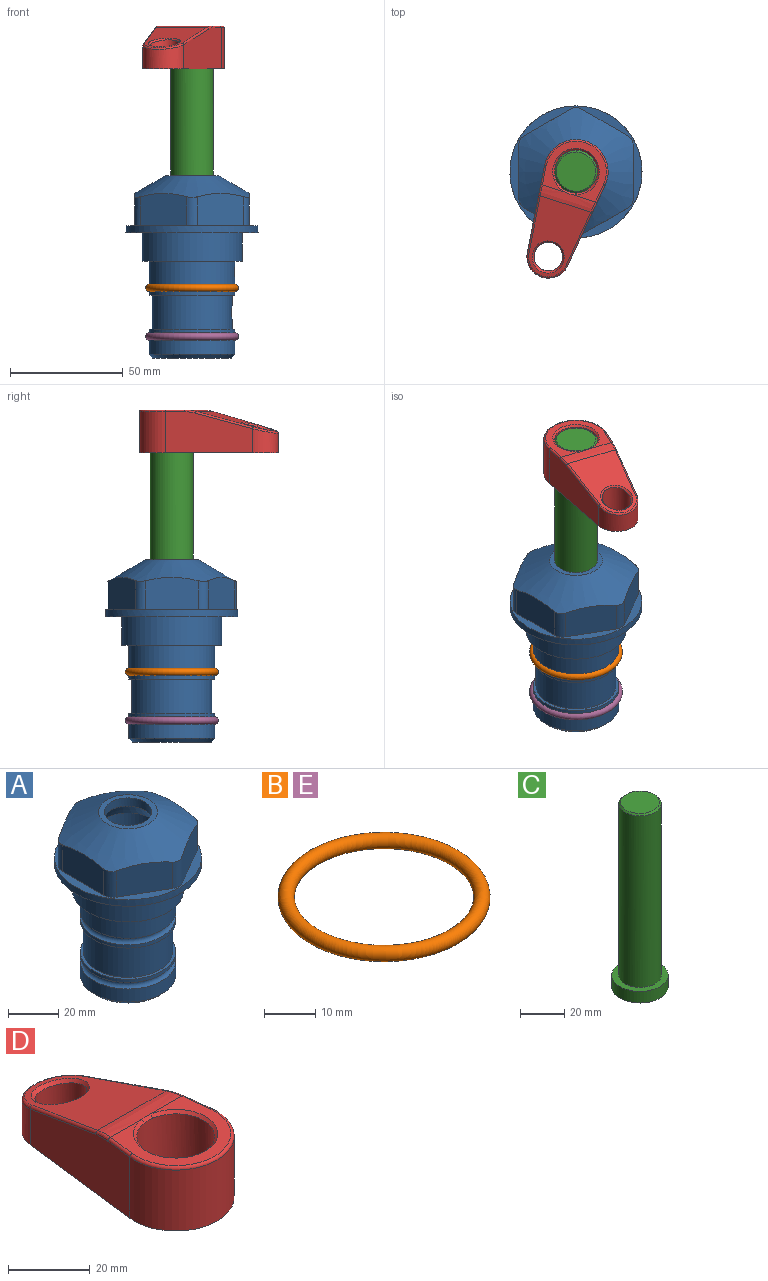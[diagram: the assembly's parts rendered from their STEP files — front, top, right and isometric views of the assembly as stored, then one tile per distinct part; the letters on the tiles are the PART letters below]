
ASSEMBLY  parts=5 mates=4
PART A: 36 faces, bbox 58.7x58.7x81 mm
  f0: cylinder r=17.78mm len=35.56mm, axis (0,0,1), area 1670.8mm2, adj f23,f24,f31
  f1: cylinder r=19.05mm len=38.1mm, axis (0,0,1), area 1191.9mm2, adj f26,f27,f30
  f2: plane 58.66x58.66mm, normal (0,0,-1), area 1150.6mm2, adj f3,f28
  f3: cylinder r=29.33mm len=58.66mm, axis (0,0,-1), area 585.1mm2, adj f2,f4
  f4: plane 58.66x58.66mm, normal (0,0,1), area 475.9mm2, adj f3,f5,f6,f7,f8,f9,f10,f11
  f5: plane 20.32x14.34mm, normal (-0.5,0.87,0), area 324.4mm2, adj f4,f15,f16,f17
  f6: plane 20.32x14.34mm, normal (0.5,0.87,0), area 324.4mm2, adj f4,f14,f15,f17
  f7: plane 23.48x14.34mm, normal (1,0,0), area 324.4mm2, adj f4,f13,f14,f17
  f8: plane 20.32x14.34mm, normal (0.5,-0.87,0), area 324.4mm2, adj f4,f12,f13,f17
  f9: plane 20.32x14.34mm, normal (-0.5,-0.87,0), area 324.4mm2, adj f4,f11,f12,f17
  f10: plane 23.48x14.34mm, normal (-1,0,0), area 324.4mm2, adj f4,f11,f16,f17
  f11: cylinder r=5.08mm len=12.85mm, axis (0,0,-1), area 67.2mm2, adj f4,f9,f10,f17
  f12: cylinder r=5.08mm len=12.85mm, axis (0,0,-1), area 67.2mm2, adj f4,f8,f9,f17
  f13: cylinder r=5.08mm len=12.85mm, axis (0,0,-1), area 67.2mm2, adj f4,f7,f8,f17
  f14: cylinder r=5.08mm len=12.85mm, axis (0,0,-1), area 67.2mm2, adj f4,f6,f7,f17
  f15: cylinder r=5.08mm len=12.85mm, axis (0,0,-1), area 67.2mm2, adj f4,f5,f6,f17
  f16: cylinder r=5.08mm len=12.85mm, axis (0,0,-1), area 67.2mm2, adj f4,f5,f10,f17
  f17: cone r=11.73mm half-angle=60deg, axis (0,0,-1), area 2071.8mm2, adj f5,f6,f7,f8,f9,f10,f11,f12
  f18: plane 23.46x23.46mm, normal (0,0,1), area 147.4mm2, adj f17,f35
  f19: plane 34.93x34.93mm, normal (0,0,-1), area 958mm2, adj f29
  f20: cylinder r=19.05mm len=38.1mm, axis (0,0,1), area 760.1mm2, adj f21,f29
  f21: torus R=19.05mm, axis (0,0,1), area 565.3mm2, adj f20,f22
  f22: cylinder r=19.05mm len=38.1mm, axis (0,0,1), area 190mm2, adj f21,f23
  f23: plane 38.1x38.1mm, normal (0,0,1), area 146.9mm2, adj f0,f22
  f24: plane 38.1x38.1mm, normal (0,0,-1), area 146.9mm2, adj f0,f25
  f25: cylinder r=19.05mm len=38.1mm, axis (0,0,1), area 190mm2, adj f24,f26
  f26: torus R=19.05mm, axis (0,0,1), area 565.3mm2, adj f1,f25
  f27: plane 44.45x44.45mm, normal (0,0,-1), area 411.7mm2, adj f1,f28
  f28: cylinder r=22.23mm len=44.45mm, axis (0,0,1), area 1773.5mm2, adj f2,f27
  f29: cone r=19.05mm half-angle=45deg, axis (0,0,1), area 257.5mm2, adj f19,f20
  f30: cylinder r=3.17mm len=6.75mm, axis (-1,0,0), area 128mm2, adj f1,f33
  f31: cylinder r=3.17mm len=6.35mm, axis (-1,0,0), area 102.5mm2, adj f0,f33
  f32: plane 25.4x25.4mm, normal (0,0,1), area 506.7mm2, adj f33
  f33: cylinder r=12.7mm len=66.42mm, axis (0,0,-1), area 5236.2mm2, adj f30,f31,f32,f34
  f34: cone r=9.53mm half-angle=30deg, axis (0,0,-1), area 443.4mm2, adj f33,f35
  f35: cylinder r=9.53mm len=19.05mm, axis (0,0,-1), area 240.9mm2, adj f18,f34
PART B: 1 faces, bbox 44.7x44.7x3.2 mm
  f0: torus R=19.05mm, axis (0,0,1), area 1193.9mm2
PART C: 6 faces, bbox 25.4x25.4x101.6 mm
  f0: plane 17.46x17.46mm, normal (0,0,1), area 239.5mm2, adj f5
  f1: plane 25.4x25.4mm, normal (0,0,-1), area 506.7mm2, adj f2
  f2: cylinder r=12.7mm len=25.4mm, axis (0,0,1), area 506.7mm2, adj f1,f3
  f3: plane 25.4x25.4mm, normal (0,0,1), area 221.7mm2, adj f2,f4
  f4: cylinder r=9.53mm len=94.46mm, axis (0,0,1), area 5653mm2, adj f3,f5
  f5: cone r=8.73mm half-angle=45deg, axis (0,0,-1), area 64.4mm2, adj f0,f4
PART D: 31 faces, bbox 31.7x65.5x19.8 mm
  f0: plane 39.12x18.26mm, normal (0.99,0.12,0), area 612.2mm2, adj f1,f4,f7,f11,f13,f15
  f1: cylinder r=9.53mm len=18.91mm, axis (0,0,-1), area 296.1mm2, adj f0,f2,f7,f17
  f2: plane 39.12x18.26mm, normal (-0.99,0.12,0), area 612.2mm2, adj f1,f4,f7,f12,f14,f16
  f3: cylinder r=6.35mm len=12.7mm, axis (0,0,-1), area 362.4mm2, adj f7,f18
  f4: cylinder r=14.29mm len=28.58mm, axis (0,0,-1), area 882.2mm2, adj f0,f2,f7,f10
  f5: cylinder r=9.53mm len=19.05mm, axis (0,0,-1), area 1092.6mm2, adj f7,f19,f20
  f6: plane 26.99x23.69mm, normal (0,0,1), area 216.2mm2, adj f9,f10,f11,f12,f19
  f7: plane 63.5x28.58mm, normal (0,0,-1), area 661.8mm2, adj f0,f1,f2,f3,f4,f5,f22,f23
  f8: plane 33.52x23.6mm, normal (0,0.26,0.97), area 486mm2, adj f9,f15,f16,f17,f18
  f9: cylinder r=19.05mm len=24.72mm, axis (1,0,0), area 120.4mm2, adj f6,f8,f13,f14,f20
  f10: torus R=13.49mm, axis (0,0,1), area 59mm2, adj f4,f6,f11,f12
  f11: cylinder r=0.79mm len=8.67mm, axis (0.12,-0.99,0), area 10.8mm2, adj f0,f6,f10,f13
  f12: cylinder r=0.79mm len=8.67mm, axis (0.12,0.99,0), area 10.8mm2, adj f2,f6,f10,f14
  f13: bspline ~4.95x1.42mm, area 6.1mm2, adj f0,f9,f11,f15
  f14: bspline ~4.95x1.42mm, area 6.1mm2, adj f2,f9,f12,f16
  f15: cylinder r=0.79mm len=25.95mm, axis (0.12,-0.96,0.26), area 32.9mm2, adj f0,f8,f13,f17
  f16: cylinder r=0.79mm len=25.95mm, axis (0.12,0.96,-0.26), area 32.9mm2, adj f2,f8,f14,f17
  f17: bspline ~18.91x8.38mm, area 30mm2, adj f1,f8,f15,f16
  f18: bspline ~14.29x14.29mm, area 48.3mm2, adj f3,f8
  f19: cone r=9.53mm half-angle=45deg, axis (0,0,1), area 66.5mm2, adj f5,f6,f20
  f20: bspline ~3.22x0.96mm, area 3.5mm2, adj f5,f9,f19
  f21: plane 2.75x2.72mm, normal (0,0,-1), area 2.9mm2, adj f23,f25,f28
  f22: plane 23.05x15.88mm, normal (-0.99,-0.12,0), area 323.6mm2, adj f7,f25,f26,f27,f28,f29
  f23: plane 23.05x15.88mm, normal (0.99,-0.12,0), area 323.6mm2, adj f7,f21,f25,f27,f28,f30
  f24: cylinder r=9.53mm len=10.69mm, axis (0,0,-1), area 114.7mm2, adj f7,f27,f29,f30
  f25: cylinder r=12.7mm len=20.59mm, axis (0,0,-1), area 381.1mm2, adj f7,f21,f22,f23,f26,f28
  f26: plane 2.75x2.72mm, normal (0,0,-1), area 2.9mm2, adj f22,f25,f28
  f27: plane 19.72x18.37mm, normal (0,-0.26,-0.97), area 291.8mm2, adj f22,f23,f24,f28,f29,f30
  f28: cylinder r=15.88mm len=19.92mm, axis (1,0,0), area 54.8mm2, adj f21,f22,f23,f25,f26,f27
  f29: cylinder r=1.59mm len=11mm, axis (0,0,-1), area 34.7mm2, adj f7,f22,f24,f27
  f30: cylinder r=1.59mm len=11mm, axis (0,0,-1), area 34.7mm2, adj f7,f23,f24,f27
PART E: same geometry as B
PLACE A at identity fixed
PLACE B at identity
PLACE C rot(axis=(0,0,1),162deg) t=(0,0,27.55)mm
PLACE D rot(axis=(0,0,1),162deg) t=(0,0,28.35)mm
PLACE E t=(0,0,-21.59)mm
MATE fastened C.f2 <-> D.f4  axis (0,0,1) through (0,0,91.05)mm
MATE fastened E.f0 <-> A.f0  axis (0,0,1) through (0,0,-46.1)mm
MATE fastened B.f0 <-> A.f0  axis (0,0,1) through (0,0,-24.51)mm
MATE cylindrical C.f2 <-> A.f0  axis (0,0,-1) through (0,0,-10.55)mm
